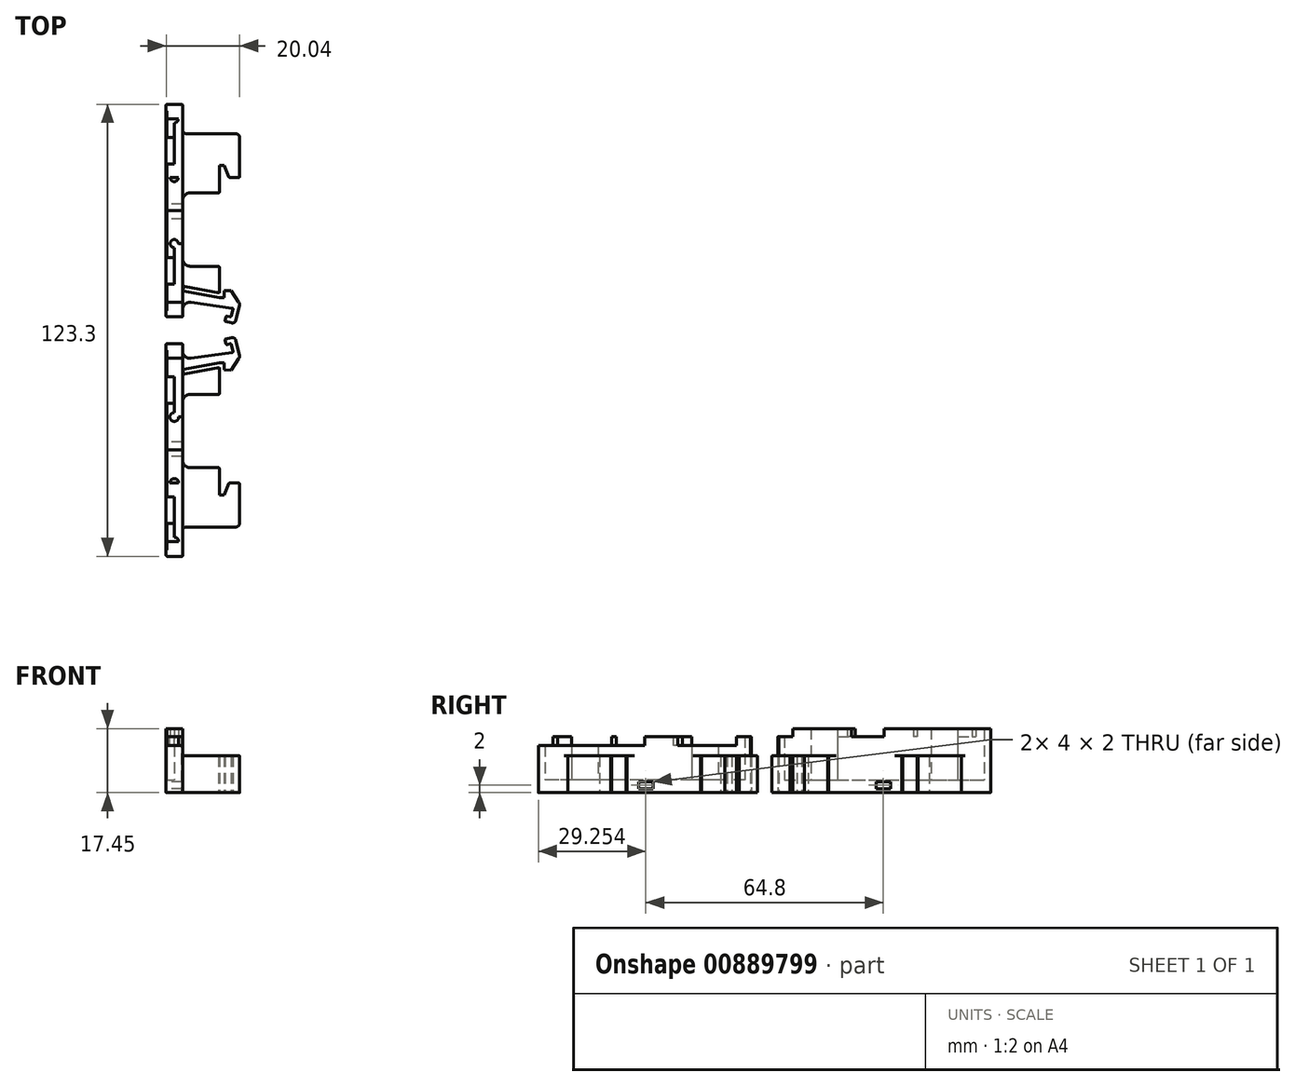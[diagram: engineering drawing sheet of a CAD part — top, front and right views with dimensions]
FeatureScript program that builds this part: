
annotation { "Feature Type Name" : "Feature", "Feature Type Description" : "" }
export const myFeature = defineFeature(function(context is Context, id is Id, definition is map)
    precondition{}
    {
        {
            var Q0;
            Q0=qCreatedBy(makeId("Top.planeOp"),FACE);
            var sketch = newSketch(context, id + "F0", { "sketchPlane" : qUnion([Q0])});
            skLineSegment(sketch, "E0.0", {"start": v(-29.42, 4.4) * mm, "end": v(-29.42, 61.9) * mm});
            skLineSegment(sketch, "E1.0", {"start": v(-29.17, 62.14) * mm, "end": v(-25.17, 62.14) * mm});
            skLineSegment(sketch, "E2.0", {"start": v(-24.92, 55.14) * mm, "end": v(-24.92, 61.9) * mm});
            skLineSegment(sketch, "E3.0", {"start": v(-10.42, 54.14) * mm, "end": v(-23.92, 54.14) * mm});
            skLineSegment(sketch, "E4.0", {"start": v(-9.42, 42.4) * mm, "end": v(-9.42, 53.14) * mm});
            skLineSegment(sketch, "E5.0", {"start": v(-12.07, 42.14) * mm, "end": v(-9.74, 42.14) * mm});
            skLineSegment(sketch, "E6.0", {"start": v(-13.67, 45.45) * mm, "end": v(-12.3, 42.3) * mm});
            skLineSegment(sketch, "E7.0", {"start": v(-14.92, 45.45) * mm, "end": v(-13.67, 45.45) * mm});
            skLineSegment(sketch, "E8.0", {"start": v(-14.92, 38.22) * mm, "end": v(-14.92, 45.45) * mm});
            skLineSegment(sketch, "E9.0", {"start": v(-15.11, 37.97) * mm, "end": v(-22.92, 37.97) * mm});
            skLineSegment(sketch, "E10.0", {"start": v(-24.92, 35.97) * mm, "end": v(-24.92, 19.97) * mm});
            skLineSegment(sketch, "E11.0", {"start": v(-15.11, 17.97) * mm, "end": v(-22.92, 17.97) * mm});
            skLineSegment(sketch, "E12.0", {"start": v(-14.92, 10.64) * mm, "end": v(-14.92, 17.72) * mm});
            skLineSegment(sketch, "E13.0", {"start": v(-14.92, 10.64) * mm, "end": v(-24.39, 12.43) * mm});
            skLineSegment(sketch, "E14.0", {"start": v(-24.82, 11.5) * mm, "end": v(-24.68, 12.23) * mm});
            skLineSegment(sketch, "E15.0", {"start": v(-14.92, 9.37) * mm, "end": v(-24.62, 11.2) * mm});
            skLineSegment(sketch, "E16.0", {"start": v(-13.67, 9.37) * mm, "end": v(-14.92, 9.37) * mm});
            skLineSegment(sketch, "E17.0", {"start": v(-13.67, 11.3) * mm, "end": v(-13.67, 9.37) * mm});
            skLineSegment(sketch, "E18.0", {"start": v(-11.67, 11.34) * mm, "end": v(-13.67, 11.3) * mm});
            skLineSegment(sketch, "E19.0", {"start": v(-11.67, 11.34) * mm, "end": v(-9.66, 8.18) * mm});
            skLineSegment(sketch, "E20.0", {"start": v(-9.38, 7.4) * mm, "end": v(-10.41, 3.24) * mm});
            skLineSegment(sketch, "E21.0", {"start": v(-11.62, 2.5) * mm, "end": v(-13.2, 2.9) * mm});
            skLineSegment(sketch, "E22.0", {"start": v(-13.38, 3.2) * mm, "end": v(-13.14, 4.17) * mm});
            skLineSegment(sketch, "E23.0", {"start": v(-12.83, 4.35) * mm, "end": v(-12, 4.14) * mm});
            skLineSegment(sketch, "E24.0", {"start": v(-11.69, 4.33) * mm, "end": v(-11.21, 6.24) * mm});
            skLineSegment(sketch, "E25.0", {"start": v(-22.65, 8.12) * mm, "end": v(-11.42, 6.55) * mm});
            skLineSegment(sketch, "E26.0", {"start": v(-24.92, 6.14) * mm, "end": v(-24.92, 4.4) * mm});
            skLineSegment(sketch, "E27.0", {"start": v(-25.26, 4.14) * mm, "end": v(-29.17, 4.14) * mm});
            skArc(sketch, "E28.0", {"start": v(-29.17, 62.14) * mm, "mid": v(-29.35, 62.07) * mm, "end": v(-29.42, 61.9) * mm});
            skArc(sketch, "E29.0", {"start": v(-24.92, 61.9) * mm, "mid": v(-25, 62.07) * mm, "end": v(-25.17, 62.14) * mm});
            skArc(sketch, "E30.0", {"start": v(-24.92, 55.14) * mm, "mid": v(-24.63, 54.44) * mm, "end": v(-23.92, 54.14) * mm});
            skArc(sketch, "E31.0", {"start": v(-9.42, 53.14) * mm, "mid": v(-9.72, 53.85) * mm, "end": v(-10.42, 54.14) * mm});
            skArc(sketch, "E32.0", {"start": v(-9.74, 42.14) * mm, "mid": v(-9.52, 42.2) * mm, "end": v(-9.42, 42.4) * mm});
            skArc(sketch, "E33.0", {"start": v(-12.3, 42.3) * mm, "mid": v(-12.2, 42.18) * mm, "end": v(-12.07, 42.14) * mm});
            skArc(sketch, "E34.0", {"start": v(-15.11, 37.97) * mm, "mid": v(-14.97, 38.07) * mm, "end": v(-14.92, 38.22) * mm});
            skArc(sketch, "E35.0", {"start": v(-22.92, 37.97) * mm, "mid": v(-24.34, 37.39) * mm, "end": v(-24.92, 35.97) * mm});
            skArc(sketch, "E36.0", {"start": v(-24.92, 19.97) * mm, "mid": v(-24.34, 18.56) * mm, "end": v(-22.92, 17.97) * mm});
            skArc(sketch, "E37.0", {"start": v(-14.92, 17.72) * mm, "mid": v(-14.97, 17.88) * mm, "end": v(-15.11, 17.97) * mm});
            skArc(sketch, "E38.0", {"start": v(-24.39, 12.43) * mm, "mid": v(-24.58, 12.39) * mm, "end": v(-24.68, 12.23) * mm});
            skArc(sketch, "E39.0", {"start": v(-24.82, 11.5) * mm, "mid": v(-24.78, 11.3) * mm, "end": v(-24.62, 11.2) * mm});
            skArc(sketch, "E40.0", {"start": v(-9.38, 7.4) * mm, "mid": v(-9.43, 7.82) * mm, "end": v(-9.66, 8.18) * mm});
            skArc(sketch, "E41.0", {"start": v(-11.62, 2.5) * mm, "mid": v(-10.87, 2.62) * mm, "end": v(-10.41, 3.24) * mm});
            skArc(sketch, "E42.0", {"start": v(-13.38, 3.2) * mm, "mid": v(-13.35, 3.01) * mm, "end": v(-13.2, 2.9) * mm});
            skArc(sketch, "E43.0", {"start": v(-12.83, 4.35) * mm, "mid": v(-13.02, 4.32) * mm, "end": v(-13.14, 4.17) * mm});
            skArc(sketch, "E44.0", {"start": v(-12, 4.14) * mm, "mid": v(-11.8, 4.17) * mm, "end": v(-11.69, 4.33) * mm});
            skArc(sketch, "E45.0", {"start": v(-11.21, 6.24) * mm, "mid": v(-11.25, 6.44) * mm, "end": v(-11.42, 6.55) * mm});
            skArc(sketch, "E46.0", {"start": v(-22.65, 8.12) * mm, "mid": v(-24.24, 7.65) * mm, "end": v(-24.92, 6.14) * mm});
            skArc(sketch, "E47.0", {"start": v(-25.26, 4.14) * mm, "mid": v(-25.02, 4.18) * mm, "end": v(-24.92, 4.4) * mm});
            skArc(sketch, "E48.0", {"start": v(-29.42, 4.4) * mm, "mid": v(-29.35, 4.22) * mm, "end": v(-29.17, 4.14) * mm});
            skLineSegment(sketch, "E49", {"start": v(-24.92, 61.9) * mm, "end": v(-24.92, 4.4) * mm});
            skLineSegment(sketch, "E50", {"start": v(-29.42, 4.4) * mm, "end": v(-29.42, 5.9) * mm});
            skLineSegment(sketch, "E51", {"start": v(-29.42, 5.9) * mm, "end": v(-29.17, 5.9) * mm});
            skLineSegment(sketch, "E52", {"start": v(-29.17, 5.9) * mm, "end": v(-29.17, 60.4) * mm});
            skLineSegment(sketch, "E53", {"start": v(-29.17, 60.4) * mm, "end": v(-29.42, 60.4) * mm});
            skLineSegment(sketch, "E54", {"start": v(-29.42, 4.4) * mm, "end": v(-29.42, 13.14) * mm});
            skLineSegment(sketch, "E55", {"start": v(-29.42, 13.14) * mm, "end": v(-27.17, 13.14) * mm});
            skLineSegment(sketch, "E56", {"start": v(-27.17, 13.14) * mm, "end": v(-27.17, 20.4) * mm});
            skLineSegment(sketch, "E57", {"start": v(-27.17, 20.4) * mm, "end": v(-29.42, 20.4) * mm});
            skLineSegment(sketch, "E58", {"start": v(-29.42, 20.4) * mm, "end": v(-29.42, 45.9) * mm});
            skLineSegment(sketch, "E59", {"start": v(-29.42, 45.9) * mm, "end": v(-27.17, 45.9) * mm});
            skLineSegment(sketch, "E60", {"start": v(-27.17, 45.9) * mm, "end": v(-27.17, 53.14) * mm});
            skLineSegment(sketch, "E61", {"start": v(-27.17, 53.14) * mm, "end": v(-29.42, 53.14) * mm});
            skSolve(sketch);
        }
        {
            var Q0;
            Q0=makeQuery(id+"F0.imprint","IMPRINT",FACE,{"disambiguationData":[TD([[makeQuery(id+"F0.imprint","IMPRINT",EDGE,{"derivedFrom":sQuery(id+"F0.wireOp",EDGE,"E3.0")}),1.0]])]});
            var Q1;
            Q1=makeQuery(id+"F0.imprint","IMPRINT",FACE,{"disambiguationData":[TD([[makeQuery(id+"F0.imprint","IMPRINT",EDGE,{"derivedFrom":sQuery(id+"F0.wireOp",EDGE,"E0.0")}),-1.0]])]});
            var Q2;
            Q2=makeQuery(id+"F0.imprint","IMPRINT",FACE,{"disambiguationData":[TD([[makeQuery(id+"F0.imprint","IMPRINT",EDGE,{"derivedFrom":sQuery(id+"F0.wireOp",EDGE,"E11.0")}),1.0]])]});
            var Q3;
            {var subQ0=sQuery(id+"F0.wireOp",EDGE,"E51");Q3=makeQuery(id+"F0.imprint","IMPRINT",FACE,{"disambiguationData":[TD([[makeQuery(id+"F0.imprint","IMPRINT",EDGE,{"derivedFrom":subQ0}),1.0]])]});}
            var Q4;
            Q4=makeQuery(id+"F0.imprint","IMPRINT",FACE,{"disambiguationData":[TD([[makeQuery(id+"F0.imprint","IMPRINT",EDGE,{"derivedFrom":sQuery(id+"F0.wireOp",EDGE,"E1.0")}),-1.0]])]});
            var Q5;
            {var subQ5=sQuery(id+"F0.wireOp",EDGE,"CiznJIct-Pn10-4pcS-3v3k-Jn6uBiTixD0h");Q5=makeQuery(id+"F0.imprint","IMPRINT",FACE,{"disambiguationData":[TD([[makeQuery(id+"F0.imprint","IMPRINT",EDGE,{"derivedFrom":subQ5}),1.0]])]});}
            var Q6;
            {var subQ5=sQuery(id+"F0.wireOp",EDGE,"xp5viDYF-1sKM-JXdj-ab4I-l8p1jcBwP8dv");Q6=makeQuery(id+"F0.imprint","IMPRINT",FACE,{"disambiguationData":[TD([[makeQuery(id+"F0.imprint","IMPRINT",EDGE,{"derivedFrom":subQ5}),1.0]])]});}
            var Q7;
            {var subQ5=sQuery(id+"F0.wireOp",EDGE,"eO4NTHjU-XLBs-ehTP-7UjW-MYbdzHAm4Ady");Q7=makeQuery(id+"F0.imprint","IMPRINT",FACE,{"disambiguationData":[TD([[makeQuery(id+"F0.imprint","IMPRINT",EDGE,{"derivedFrom":subQ5}),-1.0]])]});}
            var Q8;
            {var subQ5=sQuery(id+"F0.wireOp",EDGE,"E56");Q8=makeQuery(id+"F0.imprint","IMPRINT",FACE,{"disambiguationData":[TD([[makeQuery(id+"F0.imprint","IMPRINT",EDGE,{"derivedFrom":subQ5}),1.0]])]});}
            var Q9;
            {var subQ5=sQuery(id+"F0.wireOp",EDGE,"E60");Q9=makeQuery(id+"F0.imprint","IMPRINT",FACE,{"disambiguationData":[TD([[makeQuery(id+"F0.imprint","IMPRINT",EDGE,{"derivedFrom":subQ5}),1.0]])]});}
            var Q10;
            {var subQ5=sQuery(id+"F0.wireOp",EDGE,"E58");Q10=makeQuery(id+"F0.imprint","IMPRINT",FACE,{"disambiguationData":[TD([[makeQuery(id+"F0.imprint","IMPRINT",EDGE,{"derivedFrom":subQ5}),-1.0]])]});}
            extrude(context, id + "F1", {"entities" : qUnion([Q0, Q1, Q2, Q3, Q4, Q5, Q6, Q7, Q8, Q9, Q10]), "depth" : 3.5 * mm, "offsetDistance" : 25 * mm});
        }
        {
            var Q0;
            Q0=makeQuery(id+"F1.opExtrude","SWEPT_FACE",FACE,{"disambiguationData":[OSD([sQuery(id+"F0.wireOp",EDGE,"E0.0")])]});
            var sketch = newSketch(context, id + "F2", { "sketchPlane" : qUnion([Q0])});
            skLineSegment(sketch, "E62.bottom", {"start": v(-30.9, 1) * mm, "end": v(-34.9, 1) * mm});
            skLineSegment(sketch, "E62.top", {"start": v(-30.9, 3) * mm, "end": v(-34.9, 3) * mm});
            skLineSegment(sketch, "E62.left", {"start": v(-30.9, 1) * mm, "end": v(-30.9, 3) * mm});
            skLineSegment(sketch, "E62.right", {"start": v(-34.9, 1) * mm, "end": v(-34.9, 3) * mm});
            skPoint(sketch, "E62.middle", {"position": v(-32.9, 2) * mm});
            skSolve(sketch);
        }
        {
            var Q0;
            Q0 = qSketchRegion(id + "F2", true);
            extrude(context, id + "F3", {"entities" : qUnion([Q0]), "operationType" : NewBodyOperationType.REMOVE, "oppositeDirection" : true, "depth" : 4.5 * mm, "offsetDistance" : 25 * mm});
        }
        {
            var Q0;
            Q0=makeQuery(id+"F1.opExtrude","CAP_FACE",FACE,{"disambiguationData":[OSD([sQuery(id+"F0.wireOp",EDGE,"E0.0"),sQuery(id+"F0.wireOp",EDGE,"E1.0"),sQuery(id+"F0.wireOp",EDGE,"E3.0"),sQuery(id+"F0.wireOp",EDGE,"E4.0"),sQuery(id+"F0.wireOp",EDGE,"E5.0"),sQuery(id+"F0.wireOp",EDGE,"E6.0"),sQuery(id+"F0.wireOp",EDGE,"E7.0"),sQuery(id+"F0.wireOp",EDGE,"E8.0"),sQuery(id+"F0.wireOp",EDGE,"E9.0"),sQuery(id+"F0.wireOp",EDGE,"E11.0"),sQuery(id+"F0.wireOp",EDGE,"E12.0"),sQuery(id+"F0.wireOp",EDGE,"E13.0"),sQuery(id+"F0.wireOp",EDGE,"E14.0"),sQuery(id+"F0.wireOp",EDGE,"E15.0"),sQuery(id+"F0.wireOp",EDGE,"E16.0"),sQuery(id+"F0.wireOp",EDGE,"E17.0"),sQuery(id+"F0.wireOp",EDGE,"E18.0"),sQuery(id+"F0.wireOp",EDGE,"E19.0"),sQuery(id+"F0.wireOp",EDGE,"E20.0"),sQuery(id+"F0.wireOp",EDGE,"E21.0"),sQuery(id+"F0.wireOp",EDGE,"E22.0"),sQuery(id+"F0.wireOp",EDGE,"E23.0"),sQuery(id+"F0.wireOp",EDGE,"E24.0"),sQuery(id+"F0.wireOp",EDGE,"E25.0"),sQuery(id+"F0.wireOp",EDGE,"E27.0"),sQuery(id+"F0.wireOp",EDGE,"E28.0"),sQuery(id+"F0.wireOp",EDGE,"E29.0"),sQuery(id+"F0.wireOp",EDGE,"E30.0"),sQuery(id+"F0.wireOp",EDGE,"E31.0"),sQuery(id+"F0.wireOp",EDGE,"E32.0"),sQuery(id+"F0.wireOp",EDGE,"E33.0"),sQuery(id+"F0.wireOp",EDGE,"E34.0"),sQuery(id+"F0.wireOp",EDGE,"E35.0"),sQuery(id+"F0.wireOp",EDGE,"E36.0"),sQuery(id+"F0.wireOp",EDGE,"E37.0"),sQuery(id+"F0.wireOp",EDGE,"E38.0"),sQuery(id+"F0.wireOp",EDGE,"E39.0"),sQuery(id+"F0.wireOp",EDGE,"E40.0"),sQuery(id+"F0.wireOp",EDGE,"E41.0"),sQuery(id+"F0.wireOp",EDGE,"E42.0"),sQuery(id+"F0.wireOp",EDGE,"E43.0"),sQuery(id+"F0.wireOp",EDGE,"E44.0"),sQuery(id+"F0.wireOp",EDGE,"E45.0"),sQuery(id+"F0.wireOp",EDGE,"E46.0"),sQuery(id+"F0.wireOp",EDGE,"E47.0"),sQuery(id+"F0.wireOp",EDGE,"E48.0"),sQuery(id+"F0.wireOp",EDGE,"E49"),sQuery(id+"F0.wireOp",EDGE,"E54"),sQuery(id+"F0.wireOp",EDGE,"eO4NTHjU-XLBs-ehTP-7UjW-MYbdzHAm4Ady")])],"isStart":false});
            var sketch = newSketch(context, id + "F4", { "sketchPlane" : qUnion([Q0])});
            skLineSegment(sketch, "E63.0", {"start": v(-29.17, 5.9) * mm, "end": v(-29.17, 60.4) * mm});
            skLineSegment(sketch, "E64.0", {"start": v(-29.42, 5.9) * mm, "end": v(-29.17, 5.9) * mm});
            skLineSegment(sketch, "E65.0", {"start": v(-29.17, 60.4) * mm, "end": v(-29.42, 60.4) * mm});
            skPoint(sketch, "E66.0", {"position": v(-28.3, 54.14) * mm});
            skLineSegment(sketch, "E67.0", {"start": v(-29.42, 13.14) * mm, "end": v(-27.17, 13.14) * mm});
            skLineSegment(sketch, "E68.0", {"start": v(-27.17, 13.14) * mm, "end": v(-27.17, 20.4) * mm});
            skLineSegment(sketch, "E69.0", {"start": v(-27.17, 20.4) * mm, "end": v(-29.42, 20.4) * mm});
            skLineSegment(sketch, "E70.0", {"start": v(-29.42, 45.9) * mm, "end": v(-27.17, 45.9) * mm});
            skLineSegment(sketch, "E71.0", {"start": v(-27.17, 45.9) * mm, "end": v(-27.17, 53.14) * mm});
            skLineSegment(sketch, "E72.0", {"start": v(-27.17, 53.14) * mm, "end": v(-29.42, 53.14) * mm});
            skSolve(sketch);
        }
        {
            var Q0;
            {var subQ12=sQuery(id+"F4.wireOp",EDGE,"E64.0");Q0=makeQuery(id+"F4.imprint","IMPRINT",FACE,{"disambiguationData":[TD([[makeQuery(id+"F4.imprint","IMPRINT",EDGE,{"derivedFrom":subQ12}),-1.0]])]});}
            extrude(context, id + "F5", {"entities" : qUnion([Q0]), "operationType" : NewBodyOperationType.ADD, "depth" : 6.5 * mm, "offsetDistance" : 25 * mm});
        }
        {
            var Q0;
            Q0=makeQuery(id+"F5.opExtrude","CAP_FACE",FACE,{"disambiguationData":[OSD([sQuery(id+"F0.wireOp",EDGE,"E0.0"),sQuery(id+"F0.wireOp",EDGE,"E1.0"),sQuery(id+"F0.wireOp",EDGE,"E3.0"),sQuery(id+"F0.wireOp",EDGE,"E4.0"),sQuery(id+"F0.wireOp",EDGE,"E5.0"),sQuery(id+"F0.wireOp",EDGE,"E6.0"),sQuery(id+"F0.wireOp",EDGE,"E7.0"),sQuery(id+"F0.wireOp",EDGE,"E8.0"),sQuery(id+"F0.wireOp",EDGE,"E9.0"),sQuery(id+"F0.wireOp",EDGE,"E11.0"),sQuery(id+"F0.wireOp",EDGE,"E12.0"),sQuery(id+"F0.wireOp",EDGE,"E13.0"),sQuery(id+"F0.wireOp",EDGE,"E14.0"),sQuery(id+"F0.wireOp",EDGE,"E15.0"),sQuery(id+"F0.wireOp",EDGE,"E16.0"),sQuery(id+"F0.wireOp",EDGE,"E17.0"),sQuery(id+"F0.wireOp",EDGE,"E18.0"),sQuery(id+"F0.wireOp",EDGE,"E19.0"),sQuery(id+"F0.wireOp",EDGE,"E20.0"),sQuery(id+"F0.wireOp",EDGE,"E21.0"),sQuery(id+"F0.wireOp",EDGE,"E22.0"),sQuery(id+"F0.wireOp",EDGE,"E23.0"),sQuery(id+"F0.wireOp",EDGE,"E24.0"),sQuery(id+"F0.wireOp",EDGE,"E25.0"),sQuery(id+"F0.wireOp",EDGE,"E27.0"),sQuery(id+"F0.wireOp",EDGE,"E28.0"),sQuery(id+"F0.wireOp",EDGE,"E29.0"),sQuery(id+"F0.wireOp",EDGE,"E30.0"),sQuery(id+"F0.wireOp",EDGE,"E31.0"),sQuery(id+"F0.wireOp",EDGE,"E32.0"),sQuery(id+"F0.wireOp",EDGE,"E33.0"),sQuery(id+"F0.wireOp",EDGE,"E34.0"),sQuery(id+"F0.wireOp",EDGE,"E35.0"),sQuery(id+"F0.wireOp",EDGE,"E36.0"),sQuery(id+"F0.wireOp",EDGE,"E37.0"),sQuery(id+"F0.wireOp",EDGE,"E38.0"),sQuery(id+"F0.wireOp",EDGE,"E39.0"),sQuery(id+"F0.wireOp",EDGE,"E40.0"),sQuery(id+"F0.wireOp",EDGE,"E41.0"),sQuery(id+"F0.wireOp",EDGE,"E42.0"),sQuery(id+"F0.wireOp",EDGE,"E43.0"),sQuery(id+"F0.wireOp",EDGE,"E44.0"),sQuery(id+"F0.wireOp",EDGE,"E45.0"),sQuery(id+"F0.wireOp",EDGE,"E46.0"),sQuery(id+"F0.wireOp",EDGE,"E47.0"),sQuery(id+"F0.wireOp",EDGE,"E48.0"),sQuery(id+"F0.wireOp",EDGE,"E49"),sQuery(id+"F0.wireOp",EDGE,"E54"),sQuery(id+"F0.wireOp",EDGE,"eO4NTHjU-XLBs-ehTP-7UjW-MYbdzHAm4Ady"),sQuery(id+"F4.wireOp",EDGE,"E63.0"),sQuery(id+"F4.wireOp",EDGE,"E64.0"),sQuery(id+"F4.wireOp",EDGE,"E65.0"),sQuery(id+"F4.wireOp",EDGE,"70bcd36a-43df-4478-8c9e-d5456ba7c832.0"),sQuery(id+"F4.wireOp",EDGE,"bf217143-492d-4eb7-9494-7eafc8b65626.0"),sQuery(id+"F4.wireOp",EDGE,"a46a1f45-c3d6-4197-9e03-8490d21bd8d4.0"),sQuery(id+"F4.wireOp",EDGE,"a334625e-ec4d-4089-b1dc-05afd864aa37.0"),sQuery(id+"F4.wireOp",EDGE,"6e801660-dba5-42c4-9896-378528af69a1.0"),sQuery(id+"F4.wireOp",EDGE,"c2987821-0ad2-4387-8c91-164f40ca8063.0")])],"isStart":false});
            var sketch = newSketch(context, id + "F6", { "sketchPlane" : qUnion([Q0])});
            skLineSegment(sketch, "E73.0", {"start": v(-24.92, 61.9) * mm, "end": v(-24.92, 4.4) * mm});
            skSolve(sketch);
        }
        {
            var Q0;
            {var subQ8=sQuery(id+"F4.wireOp",EDGE,"E64.0");Q0=makeQuery(id+"F6.imprint","IMPRINT",FACE,{"disambiguationData":[TD([[makeQuery(id+"F6.imprint","IMPRINT",EDGE,{"derivedFrom":makeQuery(id+"F5.opExtrude","CAP_EDGE",EDGE,{"disambiguationData":[OSD([subQ8])],"isStart":false})}),-1.0]])]});}
            extrude(context, id + "F7", {"entities" : qUnion([Q0]), "operationType" : NewBodyOperationType.ADD, "depth" : 5.25 * mm, "offsetDistance" : 25 * mm});
        }
        {
            var Q0;
            Q0=makeQuery(id+"F1.opExtrude","SWEPT_BODY",BODY,{"disambiguationData":[OSD([sQuery(id+"F0.wireOp",EDGE,"E0.0"),sQuery(id+"F0.wireOp",EDGE,"E1.0"),sQuery(id+"F0.wireOp",EDGE,"E3.0"),sQuery(id+"F0.wireOp",EDGE,"E4.0"),sQuery(id+"F0.wireOp",EDGE,"E5.0"),sQuery(id+"F0.wireOp",EDGE,"E6.0"),sQuery(id+"F0.wireOp",EDGE,"E7.0"),sQuery(id+"F0.wireOp",EDGE,"E8.0"),sQuery(id+"F0.wireOp",EDGE,"E9.0"),sQuery(id+"F0.wireOp",EDGE,"E11.0"),sQuery(id+"F0.wireOp",EDGE,"E12.0"),sQuery(id+"F0.wireOp",EDGE,"E13.0"),sQuery(id+"F0.wireOp",EDGE,"E14.0"),sQuery(id+"F0.wireOp",EDGE,"E15.0"),sQuery(id+"F0.wireOp",EDGE,"E16.0"),sQuery(id+"F0.wireOp",EDGE,"E17.0"),sQuery(id+"F0.wireOp",EDGE,"E18.0"),sQuery(id+"F0.wireOp",EDGE,"E19.0"),sQuery(id+"F0.wireOp",EDGE,"E20.0"),sQuery(id+"F0.wireOp",EDGE,"E21.0"),sQuery(id+"F0.wireOp",EDGE,"E22.0"),sQuery(id+"F0.wireOp",EDGE,"E23.0"),sQuery(id+"F0.wireOp",EDGE,"E24.0"),sQuery(id+"F0.wireOp",EDGE,"E25.0"),sQuery(id+"F0.wireOp",EDGE,"E27.0"),sQuery(id+"F0.wireOp",EDGE,"E28.0"),sQuery(id+"F0.wireOp",EDGE,"E29.0"),sQuery(id+"F0.wireOp",EDGE,"E30.0"),sQuery(id+"F0.wireOp",EDGE,"E31.0"),sQuery(id+"F0.wireOp",EDGE,"E32.0"),sQuery(id+"F0.wireOp",EDGE,"E33.0"),sQuery(id+"F0.wireOp",EDGE,"E34.0"),sQuery(id+"F0.wireOp",EDGE,"E35.0"),sQuery(id+"F0.wireOp",EDGE,"E36.0"),sQuery(id+"F0.wireOp",EDGE,"E37.0"),sQuery(id+"F0.wireOp",EDGE,"E38.0"),sQuery(id+"F0.wireOp",EDGE,"E39.0"),sQuery(id+"F0.wireOp",EDGE,"E40.0"),sQuery(id+"F0.wireOp",EDGE,"E41.0"),sQuery(id+"F0.wireOp",EDGE,"E42.0"),sQuery(id+"F0.wireOp",EDGE,"E43.0"),sQuery(id+"F0.wireOp",EDGE,"E44.0"),sQuery(id+"F0.wireOp",EDGE,"E45.0"),sQuery(id+"F0.wireOp",EDGE,"E46.0"),sQuery(id+"F0.wireOp",EDGE,"E47.0"),sQuery(id+"F0.wireOp",EDGE,"E48.0"),sQuery(id+"F0.wireOp",EDGE,"E49"),sQuery(id+"F0.wireOp",EDGE,"E54"),sQuery(id+"F0.wireOp",EDGE,"eO4NTHjU-XLBs-ehTP-7UjW-MYbdzHAm4Ady")])]});
            var Q1;
            Q1=makeQuery(id+"F7.opExtrude","CAP_FACE",FACE,{"disambiguationData":[OSD([sQuery(id+"F0.wireOp",EDGE,"E0.0"),sQuery(id+"F0.wireOp",EDGE,"E1.0"),sQuery(id+"F0.wireOp",EDGE,"E27.0"),sQuery(id+"F0.wireOp",EDGE,"E28.0"),sQuery(id+"F0.wireOp",EDGE,"E29.0"),sQuery(id+"F0.wireOp",EDGE,"E47.0"),sQuery(id+"F0.wireOp",EDGE,"E48.0"),sQuery(id+"F0.wireOp",EDGE,"E54"),sQuery(id+"F0.wireOp",EDGE,"eO4NTHjU-XLBs-ehTP-7UjW-MYbdzHAm4Ady"),sQuery(id+"F4.wireOp",EDGE,"E63.0"),sQuery(id+"F4.wireOp",EDGE,"E64.0"),sQuery(id+"F4.wireOp",EDGE,"E65.0"),sQuery(id+"F4.wireOp",EDGE,"70bcd36a-43df-4478-8c9e-d5456ba7c832.0"),sQuery(id+"F4.wireOp",EDGE,"bf217143-492d-4eb7-9494-7eafc8b65626.0"),sQuery(id+"F4.wireOp",EDGE,"a46a1f45-c3d6-4197-9e03-8490d21bd8d4.0"),sQuery(id+"F4.wireOp",EDGE,"a334625e-ec4d-4089-b1dc-05afd864aa37.0"),sQuery(id+"F4.wireOp",EDGE,"6e801660-dba5-42c4-9896-378528af69a1.0"),sQuery(id+"F4.wireOp",EDGE,"c2987821-0ad2-4387-8c91-164f40ca8063.0"),sQuery(id+"F6.wireOp",EDGE,"E73.0")])],"isStart":false});
            mirror(context, id + "F8", {"entities" : qUnion([Q0]), "mirrorPlane" : qUnion([Q1])});
        }
        {
            var Q0;
            Q0=makeQuery(id+"F8.opPattern","COPY",BODY,{"derivedFrom":makeQuery(id+"F1.opExtrude","SWEPT_BODY",BODY,{"disambiguationData":[OSD([sQuery(id+"F0.wireOp",EDGE,"E0.0"),sQuery(id+"F0.wireOp",EDGE,"E1.0"),sQuery(id+"F0.wireOp",EDGE,"E3.0"),sQuery(id+"F0.wireOp",EDGE,"E4.0"),sQuery(id+"F0.wireOp",EDGE,"E5.0"),sQuery(id+"F0.wireOp",EDGE,"E6.0"),sQuery(id+"F0.wireOp",EDGE,"E7.0"),sQuery(id+"F0.wireOp",EDGE,"E8.0"),sQuery(id+"F0.wireOp",EDGE,"E9.0"),sQuery(id+"F0.wireOp",EDGE,"E11.0"),sQuery(id+"F0.wireOp",EDGE,"E12.0"),sQuery(id+"F0.wireOp",EDGE,"E13.0"),sQuery(id+"F0.wireOp",EDGE,"E14.0"),sQuery(id+"F0.wireOp",EDGE,"E15.0"),sQuery(id+"F0.wireOp",EDGE,"E16.0"),sQuery(id+"F0.wireOp",EDGE,"E17.0"),sQuery(id+"F0.wireOp",EDGE,"E18.0"),sQuery(id+"F0.wireOp",EDGE,"E19.0"),sQuery(id+"F0.wireOp",EDGE,"E20.0"),sQuery(id+"F0.wireOp",EDGE,"E21.0"),sQuery(id+"F0.wireOp",EDGE,"E22.0"),sQuery(id+"F0.wireOp",EDGE,"E23.0"),sQuery(id+"F0.wireOp",EDGE,"E24.0"),sQuery(id+"F0.wireOp",EDGE,"E25.0"),sQuery(id+"F0.wireOp",EDGE,"E27.0"),sQuery(id+"F0.wireOp",EDGE,"E28.0"),sQuery(id+"F0.wireOp",EDGE,"E29.0"),sQuery(id+"F0.wireOp",EDGE,"E30.0"),sQuery(id+"F0.wireOp",EDGE,"E31.0"),sQuery(id+"F0.wireOp",EDGE,"E32.0"),sQuery(id+"F0.wireOp",EDGE,"E33.0"),sQuery(id+"F0.wireOp",EDGE,"E34.0"),sQuery(id+"F0.wireOp",EDGE,"E35.0"),sQuery(id+"F0.wireOp",EDGE,"E36.0"),sQuery(id+"F0.wireOp",EDGE,"E37.0"),sQuery(id+"F0.wireOp",EDGE,"E38.0"),sQuery(id+"F0.wireOp",EDGE,"E39.0"),sQuery(id+"F0.wireOp",EDGE,"E40.0"),sQuery(id+"F0.wireOp",EDGE,"E41.0"),sQuery(id+"F0.wireOp",EDGE,"E42.0"),sQuery(id+"F0.wireOp",EDGE,"E43.0"),sQuery(id+"F0.wireOp",EDGE,"E44.0"),sQuery(id+"F0.wireOp",EDGE,"E45.0"),sQuery(id+"F0.wireOp",EDGE,"E46.0"),sQuery(id+"F0.wireOp",EDGE,"E47.0"),sQuery(id+"F0.wireOp",EDGE,"E48.0"),sQuery(id+"F0.wireOp",EDGE,"E49"),sQuery(id+"F0.wireOp",EDGE,"E54"),sQuery(id+"F0.wireOp",EDGE,"eO4NTHjU-XLBs-ehTP-7UjW-MYbdzHAm4Ady")])]}),"instanceName":"1"});
            var Q1;
            Q1=makeQuery(id+"F7.opExtrude","CAP_EDGE",EDGE,{"disambiguationData":[OSD([sQuery(id+"F0.wireOp",EDGE,"E1.0")])],"isStart":false});
            transform(context, id + "F9", {"entities" : qUnion([Q0]), "transformType" : TransformType.ROTATION, "transformAxis" : qUnion([Q1]), "angle" : 180 * degree, "makeCopy" : false});
        }
        {
            var Q0;
            Q0=makeQuery(id+"F8.opPattern","COPY",BODY,{"derivedFrom":makeQuery(id+"F1.opExtrude","SWEPT_BODY",BODY,{"disambiguationData":[OSD([sQuery(id+"F0.wireOp",EDGE,"E0.0"),sQuery(id+"F0.wireOp",EDGE,"E1.0"),sQuery(id+"F0.wireOp",EDGE,"E3.0"),sQuery(id+"F0.wireOp",EDGE,"E4.0"),sQuery(id+"F0.wireOp",EDGE,"E5.0"),sQuery(id+"F0.wireOp",EDGE,"E6.0"),sQuery(id+"F0.wireOp",EDGE,"E7.0"),sQuery(id+"F0.wireOp",EDGE,"E8.0"),sQuery(id+"F0.wireOp",EDGE,"E9.0"),sQuery(id+"F0.wireOp",EDGE,"E11.0"),sQuery(id+"F0.wireOp",EDGE,"E12.0"),sQuery(id+"F0.wireOp",EDGE,"E13.0"),sQuery(id+"F0.wireOp",EDGE,"E14.0"),sQuery(id+"F0.wireOp",EDGE,"E15.0"),sQuery(id+"F0.wireOp",EDGE,"E16.0"),sQuery(id+"F0.wireOp",EDGE,"E17.0"),sQuery(id+"F0.wireOp",EDGE,"E18.0"),sQuery(id+"F0.wireOp",EDGE,"E19.0"),sQuery(id+"F0.wireOp",EDGE,"E20.0"),sQuery(id+"F0.wireOp",EDGE,"E21.0"),sQuery(id+"F0.wireOp",EDGE,"E22.0"),sQuery(id+"F0.wireOp",EDGE,"E23.0"),sQuery(id+"F0.wireOp",EDGE,"E24.0"),sQuery(id+"F0.wireOp",EDGE,"E25.0"),sQuery(id+"F0.wireOp",EDGE,"E27.0"),sQuery(id+"F0.wireOp",EDGE,"E28.0"),sQuery(id+"F0.wireOp",EDGE,"E29.0"),sQuery(id+"F0.wireOp",EDGE,"E30.0"),sQuery(id+"F0.wireOp",EDGE,"E31.0"),sQuery(id+"F0.wireOp",EDGE,"E32.0"),sQuery(id+"F0.wireOp",EDGE,"E33.0"),sQuery(id+"F0.wireOp",EDGE,"E34.0"),sQuery(id+"F0.wireOp",EDGE,"E35.0"),sQuery(id+"F0.wireOp",EDGE,"E36.0"),sQuery(id+"F0.wireOp",EDGE,"E37.0"),sQuery(id+"F0.wireOp",EDGE,"E38.0"),sQuery(id+"F0.wireOp",EDGE,"E39.0"),sQuery(id+"F0.wireOp",EDGE,"E40.0"),sQuery(id+"F0.wireOp",EDGE,"E41.0"),sQuery(id+"F0.wireOp",EDGE,"E42.0"),sQuery(id+"F0.wireOp",EDGE,"E43.0"),sQuery(id+"F0.wireOp",EDGE,"E44.0"),sQuery(id+"F0.wireOp",EDGE,"E45.0"),sQuery(id+"F0.wireOp",EDGE,"E46.0"),sQuery(id+"F0.wireOp",EDGE,"E47.0"),sQuery(id+"F0.wireOp",EDGE,"E48.0"),sQuery(id+"F0.wireOp",EDGE,"E49"),sQuery(id+"F0.wireOp",EDGE,"E54"),sQuery(id+"F0.wireOp",EDGE,"eO4NTHjU-XLBs-ehTP-7UjW-MYbdzHAm4Ady")])]}),"instanceName":"1"});
            transform(context, id + "F10", {"entities" : qUnion([Q0]), "transformType" : TransformType.TRANSLATION_3D, "dx" : 0 * mm, "dy" : -123.3 * mm, "dz" : 0 * mm, "makeCopy" : false});
        }
        {
            var Q0;
            Q0=makeQuery(id+"F7.opExtrude","CAP_FACE",FACE,{"disambiguationData":[OSD([sQuery(id+"F0.wireOp",EDGE,"E0.0"),sQuery(id+"F0.wireOp",EDGE,"E1.0"),sQuery(id+"F0.wireOp",EDGE,"E27.0"),sQuery(id+"F0.wireOp",EDGE,"E28.0"),sQuery(id+"F0.wireOp",EDGE,"E29.0"),sQuery(id+"F0.wireOp",EDGE,"E47.0"),sQuery(id+"F0.wireOp",EDGE,"E48.0"),sQuery(id+"F0.wireOp",EDGE,"E54"),sQuery(id+"F0.wireOp",EDGE,"eO4NTHjU-XLBs-ehTP-7UjW-MYbdzHAm4Ady"),sQuery(id+"F4.wireOp",EDGE,"E63.0"),sQuery(id+"F4.wireOp",EDGE,"E64.0"),sQuery(id+"F4.wireOp",EDGE,"E65.0"),sQuery(id+"F4.wireOp",EDGE,"70bcd36a-43df-4478-8c9e-d5456ba7c832.0"),sQuery(id+"F4.wireOp",EDGE,"bf217143-492d-4eb7-9494-7eafc8b65626.0"),sQuery(id+"F4.wireOp",EDGE,"a46a1f45-c3d6-4197-9e03-8490d21bd8d4.0"),sQuery(id+"F4.wireOp",EDGE,"a334625e-ec4d-4089-b1dc-05afd864aa37.0"),sQuery(id+"F4.wireOp",EDGE,"6e801660-dba5-42c4-9896-378528af69a1.0"),sQuery(id+"F4.wireOp",EDGE,"c2987821-0ad2-4387-8c91-164f40ca8063.0"),sQuery(id+"F6.wireOp",EDGE,"E73.0")])],"isStart":false});
            var sketch = newSketch(context, id + "F11", { "sketchPlane" : qUnion([Q0])});
            skLineSegment(sketch, "E74", {"start": v(-27.22, 4.14) * mm, "end": v(-27.22, 62.14) * mm});
            skLineSegment(sketch, "E75", {"start": v(-24.92, 8.14) * mm, "end": v(-29.17, 8.14) * mm});
            skPoint(sketch, "E75.endSnap0", {"position": v(-29.17, 9.52) * mm});
            skLineSegment(sketch, "E76", {"start": v(-24.92, 33.14) * mm, "end": v(-29.17, 33.14) * mm});
            skLineSegment(sketch, "E77", {"start": v(-24.92, 58.14) * mm, "end": v(-29.17, 58.14) * mm});
            skPoint(sketch, "E78", {"position": v(-27.22, 8.14) * mm});
            skPoint(sketch, "E79", {"position": v(-27.22, 33.14) * mm});
            skPoint(sketch, "E80", {"position": v(-27.22, 58.14) * mm});
            skCircle(sketch, "E81", {"center": v(-27.22, 58.14) * mm, "radius": 1.1 * mm});
            skCircle(sketch, "E82", {"center": v(-27.22, 33.14) * mm, "radius": 1.1 * mm});
            skCircle(sketch, "E83", {"center": v(-27.22, 8.14) * mm, "radius": 1.1 * mm});
            skLineSegment(sketch, "E84", {"start": v(-29.17, 42.14) * mm, "end": v(-24.92, 42.14) * mm});
            skLineSegment(sketch, "E85", {"start": v(-29.17, 24.14) * mm, "end": v(-24.92, 24.14) * mm});
            skPoint(sketch, "E86", {"position": v(-27.22, 24.14) * mm});
            skPoint(sketch, "E87", {"position": v(-27.22, 42.14) * mm});
            skCircle(sketch, "E88", {"center": v(-27.22, 24.14) * mm, "radius": 1.1 * mm});
            skCircle(sketch, "E89", {"center": v(-27.22, 42.14) * mm, "radius": 1.1 * mm});
            skSolve(sketch);
        }
        {
            var Q0;
            Q0=makeQuery(id+"F8.opPattern","COPY",FACE,{"derivedFrom":makeQuery(id+"F7.opExtrude","CAP_FACE",FACE,{"disambiguationData":[OSD([sQuery(id+"F0.wireOp",EDGE,"E0.0"),sQuery(id+"F0.wireOp",EDGE,"E1.0"),sQuery(id+"F0.wireOp",EDGE,"E27.0"),sQuery(id+"F0.wireOp",EDGE,"E28.0"),sQuery(id+"F0.wireOp",EDGE,"E29.0"),sQuery(id+"F0.wireOp",EDGE,"E47.0"),sQuery(id+"F0.wireOp",EDGE,"E48.0"),sQuery(id+"F0.wireOp",EDGE,"E54"),sQuery(id+"F0.wireOp",EDGE,"eO4NTHjU-XLBs-ehTP-7UjW-MYbdzHAm4Ady"),sQuery(id+"F4.wireOp",EDGE,"E63.0"),sQuery(id+"F4.wireOp",EDGE,"E64.0"),sQuery(id+"F4.wireOp",EDGE,"E65.0"),sQuery(id+"F4.wireOp",EDGE,"70bcd36a-43df-4478-8c9e-d5456ba7c832.0"),sQuery(id+"F4.wireOp",EDGE,"bf217143-492d-4eb7-9494-7eafc8b65626.0"),sQuery(id+"F4.wireOp",EDGE,"a46a1f45-c3d6-4197-9e03-8490d21bd8d4.0"),sQuery(id+"F4.wireOp",EDGE,"a334625e-ec4d-4089-b1dc-05afd864aa37.0"),sQuery(id+"F4.wireOp",EDGE,"6e801660-dba5-42c4-9896-378528af69a1.0"),sQuery(id+"F4.wireOp",EDGE,"c2987821-0ad2-4387-8c91-164f40ca8063.0"),sQuery(id+"F6.wireOp",EDGE,"E73.0")])],"isStart":false}),"instanceName":"1"});
            var sketch = newSketch(context, id + "F12", { "sketchPlane" : qUnion([Q0])});
            skLineSegment(sketch, "E90", {"start": v(-27.22, -3.16) * mm, "end": v(-27.22, -61.16) * mm});
            skLineSegment(sketch, "E91", {"start": v(-24.92, -7.16) * mm, "end": v(-29.17, -7.16) * mm});
            skLineSegment(sketch, "E92", {"start": v(-24.92, -32.16) * mm, "end": v(-29.17, -32.16) * mm});
            skLineSegment(sketch, "E93", {"start": v(-24.92, -57.16) * mm, "end": v(-29.17, -57.16) * mm});
            skPoint(sketch, "E94", {"position": v(-27.22, -57.16) * mm});
            skPoint(sketch, "E95", {"position": v(-27.22, -32.16) * mm});
            skPoint(sketch, "E96", {"position": v(-27.22, -7.16) * mm});
            skCircle(sketch, "E97", {"center": v(-27.22, -57.16) * mm, "radius": 1.2 * mm});
            skCircle(sketch, "E98", {"center": v(-27.22, -32.16) * mm, "radius": 1.2 * mm});
            skCircle(sketch, "E99", {"center": v(-27.22, -7.16) * mm, "radius": 1.2 * mm});
            skLineSegment(sketch, "E100", {"start": v(-29.17, -41.16) * mm, "end": v(-24.92, -41.16) * mm});
            skLineSegment(sketch, "E101", {"start": v(-29.17, -23.16) * mm, "end": v(-24.92, -23.16) * mm});
            skPoint(sketch, "E102", {"position": v(-27.22, -41.16) * mm});
            skPoint(sketch, "E103", {"position": v(-27.22, -23.16) * mm});
            skCircle(sketch, "E104", {"center": v(-27.22, -41.16) * mm, "radius": 1.2 * mm});
            skCircle(sketch, "E105", {"center": v(-27.22, -23.16) * mm, "radius": 1.2 * mm});
            skSolve(sketch);
        }
        {
            var Q0;
            {var subQ0=sQuery(id+"F12.wireOp",EDGE,"E93");var subQ1=sQuery(id+"F12.wireOp",EDGE,"E90");var subQ2=makeQuery(id+"F12.imprint","INTERSECT",VERTEX,{"derivedFrom":[subQ1,subQ0]});Q0=makeQuery(id+"F12.imprint","IMPRINT",FACE,{"disambiguationData":[TD([[makeQuery(id+"F12.imprint","IMPRINT",EDGE,{"disambiguationData":[TD([[subQ2,-1.0]])],"derivedFrom":subQ1}),-1.0]])]});}
            var Q1;
            {var subQ0=sQuery(id+"F12.wireOp",EDGE,"E97");var subQ1=sQuery(id+"F12.wireOp",EDGE,"E90");var subQ2=makeQuery(id+"F12.imprint","INTERSECT",VERTEX,{"disambiguationData":[OD(0.0)],"derivedFrom":[subQ1,subQ0]});Q1=makeQuery(id+"F12.imprint","IMPRINT",FACE,{"disambiguationData":[TD([[makeQuery(id+"F12.imprint","IMPRINT",EDGE,{"disambiguationData":[TD([[subQ2,-1.0]])],"derivedFrom":subQ1}),-1.0]])]});}
            var Q2;
            {var subQ0=sQuery(id+"F12.wireOp",EDGE,"E97");var subQ1=sQuery(id+"F12.wireOp",EDGE,"E90");var subQ2=makeQuery(id+"F12.imprint","INTERSECT",VERTEX,{"disambiguationData":[OD(0.0)],"derivedFrom":[subQ1,subQ0]});Q2=makeQuery(id+"F12.imprint","IMPRINT",FACE,{"disambiguationData":[TD([[makeQuery(id+"F12.imprint","IMPRINT",EDGE,{"disambiguationData":[TD([[subQ2,-1.0]])],"derivedFrom":subQ1}),1.0]])]});}
            var Q3;
            {var subQ0=sQuery(id+"F12.wireOp",EDGE,"E93");var subQ1=sQuery(id+"F12.wireOp",EDGE,"E90");var subQ2=makeQuery(id+"F12.imprint","INTERSECT",VERTEX,{"derivedFrom":[subQ1,subQ0]});Q3=makeQuery(id+"F12.imprint","IMPRINT",FACE,{"disambiguationData":[TD([[makeQuery(id+"F12.imprint","IMPRINT",EDGE,{"disambiguationData":[TD([[subQ2,-1.0]])],"derivedFrom":subQ1}),1.0]])]});}
            var Q4;
            {var subQ0=sQuery(id+"F12.wireOp",EDGE,"E92");var subQ1=sQuery(id+"F12.wireOp",EDGE,"E90");var subQ2=makeQuery(id+"F12.imprint","INTERSECT",VERTEX,{"derivedFrom":[subQ1,subQ0]});Q4=makeQuery(id+"F12.imprint","IMPRINT",FACE,{"disambiguationData":[TD([[makeQuery(id+"F12.imprint","IMPRINT",EDGE,{"disambiguationData":[TD([[subQ2,-1.0]])],"derivedFrom":subQ1}),-1.0]])]});}
            var Q5;
            {var subQ0=sQuery(id+"F12.wireOp",EDGE,"E98");var subQ1=sQuery(id+"F12.wireOp",EDGE,"E90");var subQ2=makeQuery(id+"F12.imprint","INTERSECT",VERTEX,{"disambiguationData":[OD(0.0)],"derivedFrom":[subQ1,subQ0]});Q5=makeQuery(id+"F12.imprint","IMPRINT",FACE,{"disambiguationData":[TD([[makeQuery(id+"F12.imprint","IMPRINT",EDGE,{"disambiguationData":[TD([[subQ2,-1.0]])],"derivedFrom":subQ1}),-1.0]])]});}
            var Q6;
            {var subQ0=sQuery(id+"F12.wireOp",EDGE,"E98");var subQ1=sQuery(id+"F12.wireOp",EDGE,"E90");var subQ2=makeQuery(id+"F12.imprint","INTERSECT",VERTEX,{"disambiguationData":[OD(0.0)],"derivedFrom":[subQ1,subQ0]});Q6=makeQuery(id+"F12.imprint","IMPRINT",FACE,{"disambiguationData":[TD([[makeQuery(id+"F12.imprint","IMPRINT",EDGE,{"disambiguationData":[TD([[subQ2,-1.0]])],"derivedFrom":subQ1}),1.0]])]});}
            var Q7;
            {var subQ0=sQuery(id+"F12.wireOp",EDGE,"E92");var subQ1=sQuery(id+"F12.wireOp",EDGE,"E90");var subQ2=makeQuery(id+"F12.imprint","INTERSECT",VERTEX,{"derivedFrom":[subQ1,subQ0]});Q7=makeQuery(id+"F12.imprint","IMPRINT",FACE,{"disambiguationData":[TD([[makeQuery(id+"F12.imprint","IMPRINT",EDGE,{"disambiguationData":[TD([[subQ2,-1.0]])],"derivedFrom":subQ1}),1.0]])]});}
            var Q8;
            {var subQ0=sQuery(id+"F12.wireOp",EDGE,"E91");var subQ1=sQuery(id+"F12.wireOp",EDGE,"E90");var subQ2=makeQuery(id+"F12.imprint","INTERSECT",VERTEX,{"derivedFrom":[subQ1,subQ0]});Q8=makeQuery(id+"F12.imprint","IMPRINT",FACE,{"disambiguationData":[TD([[makeQuery(id+"F12.imprint","IMPRINT",EDGE,{"disambiguationData":[TD([[subQ2,-1.0]])],"derivedFrom":subQ1}),-1.0]])]});}
            var Q9;
            {var subQ0=sQuery(id+"F12.wireOp",EDGE,"E99");var subQ1=sQuery(id+"F12.wireOp",EDGE,"E90");var subQ2=makeQuery(id+"F12.imprint","INTERSECT",VERTEX,{"disambiguationData":[OD(0.0)],"derivedFrom":[subQ1,subQ0]});Q9=makeQuery(id+"F12.imprint","IMPRINT",FACE,{"disambiguationData":[TD([[makeQuery(id+"F12.imprint","IMPRINT",EDGE,{"disambiguationData":[TD([[subQ2,-1.0]])],"derivedFrom":subQ1}),-1.0]])]});}
            var Q10;
            {var subQ0=sQuery(id+"F12.wireOp",EDGE,"E99");var subQ1=sQuery(id+"F12.wireOp",EDGE,"E90");var subQ2=makeQuery(id+"F12.imprint","INTERSECT",VERTEX,{"disambiguationData":[OD(0.0)],"derivedFrom":[subQ1,subQ0]});Q10=makeQuery(id+"F12.imprint","IMPRINT",FACE,{"disambiguationData":[TD([[makeQuery(id+"F12.imprint","IMPRINT",EDGE,{"disambiguationData":[TD([[subQ2,-1.0]])],"derivedFrom":subQ1}),1.0]])]});}
            var Q11;
            {var subQ0=sQuery(id+"F12.wireOp",EDGE,"E91");var subQ1=sQuery(id+"F12.wireOp",EDGE,"E90");var subQ2=makeQuery(id+"F12.imprint","INTERSECT",VERTEX,{"derivedFrom":[subQ1,subQ0]});Q11=makeQuery(id+"F12.imprint","IMPRINT",FACE,{"disambiguationData":[TD([[makeQuery(id+"F12.imprint","IMPRINT",EDGE,{"disambiguationData":[TD([[subQ2,-1.0]])],"derivedFrom":subQ1}),1.0]])]});}
            var Q12;
            {var subQ0=sQuery(id+"F12.wireOp",EDGE,"E104");var subQ1=sQuery(id+"F12.wireOp",EDGE,"E90");var subQ2=makeQuery(id+"F12.imprint","INTERSECT",VERTEX,{"disambiguationData":[OD(0.0)],"derivedFrom":[subQ1,subQ0]});Q12=makeQuery(id+"F12.imprint","IMPRINT",FACE,{"disambiguationData":[TD([[makeQuery(id+"F12.imprint","IMPRINT",EDGE,{"disambiguationData":[TD([[subQ2,-1.0]])],"derivedFrom":subQ1}),-1.0]])]});}
            var Q13;
            {var subQ0=sQuery(id+"F12.wireOp",EDGE,"E100");var subQ1=sQuery(id+"F12.wireOp",EDGE,"E90");var subQ2=makeQuery(id+"F12.imprint","INTERSECT",VERTEX,{"derivedFrom":[subQ1,subQ0]});Q13=makeQuery(id+"F12.imprint","IMPRINT",FACE,{"disambiguationData":[TD([[makeQuery(id+"F12.imprint","IMPRINT",EDGE,{"disambiguationData":[TD([[subQ2,-1.0]])],"derivedFrom":subQ1}),-1.0]])]});}
            var Q14;
            {var subQ0=sQuery(id+"F12.wireOp",EDGE,"E100");var subQ1=sQuery(id+"F12.wireOp",EDGE,"E90");var subQ2=makeQuery(id+"F12.imprint","INTERSECT",VERTEX,{"derivedFrom":[subQ1,subQ0]});Q14=makeQuery(id+"F12.imprint","IMPRINT",FACE,{"disambiguationData":[TD([[makeQuery(id+"F12.imprint","IMPRINT",EDGE,{"disambiguationData":[TD([[subQ2,-1.0]])],"derivedFrom":subQ1}),1.0]])]});}
            var Q15;
            {var subQ0=sQuery(id+"F12.wireOp",EDGE,"E104");var subQ1=sQuery(id+"F12.wireOp",EDGE,"E90");var subQ2=makeQuery(id+"F12.imprint","INTERSECT",VERTEX,{"disambiguationData":[OD(0.0)],"derivedFrom":[subQ1,subQ0]});Q15=makeQuery(id+"F12.imprint","IMPRINT",FACE,{"disambiguationData":[TD([[makeQuery(id+"F12.imprint","IMPRINT",EDGE,{"disambiguationData":[TD([[subQ2,-1.0]])],"derivedFrom":subQ1}),1.0]])]});}
            var Q16;
            {var subQ0=sQuery(id+"F12.wireOp",EDGE,"E101");var subQ1=sQuery(id+"F12.wireOp",EDGE,"E90");var subQ2=makeQuery(id+"F12.imprint","INTERSECT",VERTEX,{"derivedFrom":[subQ1,subQ0]});Q16=makeQuery(id+"F12.imprint","IMPRINT",FACE,{"disambiguationData":[TD([[makeQuery(id+"F12.imprint","IMPRINT",EDGE,{"disambiguationData":[TD([[subQ2,-1.0]])],"derivedFrom":subQ1}),1.0]])]});}
            var Q17;
            {var subQ0=sQuery(id+"F12.wireOp",EDGE,"E105");var subQ1=sQuery(id+"F12.wireOp",EDGE,"E90");var subQ2=makeQuery(id+"F12.imprint","INTERSECT",VERTEX,{"disambiguationData":[OD(0.0)],"derivedFrom":[subQ1,subQ0]});Q17=makeQuery(id+"F12.imprint","IMPRINT",FACE,{"disambiguationData":[TD([[makeQuery(id+"F12.imprint","IMPRINT",EDGE,{"disambiguationData":[TD([[subQ2,-1.0]])],"derivedFrom":subQ1}),1.0]])]});}
            var Q18;
            {var subQ0=sQuery(id+"F12.wireOp",EDGE,"E105");var subQ1=sQuery(id+"F12.wireOp",EDGE,"E90");var subQ2=makeQuery(id+"F12.imprint","INTERSECT",VERTEX,{"disambiguationData":[OD(0.0)],"derivedFrom":[subQ1,subQ0]});Q18=makeQuery(id+"F12.imprint","IMPRINT",FACE,{"disambiguationData":[TD([[makeQuery(id+"F12.imprint","IMPRINT",EDGE,{"disambiguationData":[TD([[subQ2,-1.0]])],"derivedFrom":subQ1}),-1.0]])]});}
            var Q19;
            {var subQ0=sQuery(id+"F12.wireOp",EDGE,"E101");var subQ1=sQuery(id+"F12.wireOp",EDGE,"E90");var subQ2=makeQuery(id+"F12.imprint","INTERSECT",VERTEX,{"derivedFrom":[subQ1,subQ0]});Q19=makeQuery(id+"F12.imprint","IMPRINT",FACE,{"disambiguationData":[TD([[makeQuery(id+"F12.imprint","IMPRINT",EDGE,{"disambiguationData":[TD([[subQ2,-1.0]])],"derivedFrom":subQ1}),-1.0]])]});}
            extrude(context, id + "F13", {"entities" : qUnion([Q0, Q1, Q2, Q3, Q4, Q5, Q6, Q7, Q8, Q9, Q10, Q11, Q12, Q13, Q14, Q15, Q16, Q17, Q18, Q19]), "operationType" : NewBodyOperationType.REMOVE, "oppositeDirection" : true, "depth" : 2.4 * mm, "offsetDistance" : 25 * mm});
        }
        {
            var Q0;
            {var subQ0=sQuery(id+"F11.wireOp",EDGE,"E82");var subQ1=sQuery(id+"F11.wireOp",EDGE,"E74");var subQ2=makeQuery(id+"F11.imprint","INTERSECT",VERTEX,{"disambiguationData":[OD(0.0)],"derivedFrom":[subQ1,subQ0]});Q0=makeQuery(id+"F11.imprint","IMPRINT",FACE,{"disambiguationData":[TD([[makeQuery(id+"F11.imprint","IMPRINT",EDGE,{"disambiguationData":[TD([[subQ2,-1.0]])],"derivedFrom":subQ1}),1.0]])]});}
            var Q1;
            {var subQ0=sQuery(id+"F11.wireOp",EDGE,"E76");var subQ1=sQuery(id+"F11.wireOp",EDGE,"E74");var subQ2=makeQuery(id+"F11.imprint","INTERSECT",VERTEX,{"derivedFrom":[subQ1,subQ0]});Q1=makeQuery(id+"F11.imprint","IMPRINT",FACE,{"disambiguationData":[TD([[makeQuery(id+"F11.imprint","IMPRINT",EDGE,{"disambiguationData":[TD([[subQ2,-1.0]])],"derivedFrom":subQ1}),1.0]])]});}
            var Q2;
            {var subQ0=sQuery(id+"F11.wireOp",EDGE,"E76");var subQ1=sQuery(id+"F11.wireOp",EDGE,"E74");var subQ2=makeQuery(id+"F11.imprint","INTERSECT",VERTEX,{"derivedFrom":[subQ1,subQ0]});Q2=makeQuery(id+"F11.imprint","IMPRINT",FACE,{"disambiguationData":[TD([[makeQuery(id+"F11.imprint","IMPRINT",EDGE,{"disambiguationData":[TD([[subQ2,-1.0]])],"derivedFrom":subQ1}),-1.0]])]});}
            var Q3;
            {var subQ0=sQuery(id+"F11.wireOp",EDGE,"E82");var subQ1=sQuery(id+"F11.wireOp",EDGE,"E74");var subQ2=makeQuery(id+"F11.imprint","INTERSECT",VERTEX,{"disambiguationData":[OD(0.0)],"derivedFrom":[subQ1,subQ0]});Q3=makeQuery(id+"F11.imprint","IMPRINT",FACE,{"disambiguationData":[TD([[makeQuery(id+"F11.imprint","IMPRINT",EDGE,{"disambiguationData":[TD([[subQ2,-1.0]])],"derivedFrom":subQ1}),-1.0]])]});}
            var Q4;
            {var subQ0=sQuery(id+"F11.wireOp",EDGE,"E77");var subQ1=sQuery(id+"F11.wireOp",EDGE,"E74");var subQ2=makeQuery(id+"F11.imprint","INTERSECT",VERTEX,{"derivedFrom":[subQ1,subQ0]});Q4=makeQuery(id+"F11.imprint","IMPRINT",FACE,{"disambiguationData":[TD([[makeQuery(id+"F11.imprint","IMPRINT",EDGE,{"disambiguationData":[TD([[subQ2,-1.0]])],"derivedFrom":subQ1}),1.0]])]});}
            var Q5;
            {var subQ0=sQuery(id+"F11.wireOp",EDGE,"E81");var subQ1=sQuery(id+"F11.wireOp",EDGE,"E74");var subQ2=makeQuery(id+"F11.imprint","INTERSECT",VERTEX,{"disambiguationData":[OD(0.0)],"derivedFrom":[subQ1,subQ0]});Q5=makeQuery(id+"F11.imprint","IMPRINT",FACE,{"disambiguationData":[TD([[makeQuery(id+"F11.imprint","IMPRINT",EDGE,{"disambiguationData":[TD([[subQ2,-1.0]])],"derivedFrom":subQ1}),1.0]])]});}
            var Q6;
            {var subQ0=sQuery(id+"F11.wireOp",EDGE,"E81");var subQ1=sQuery(id+"F11.wireOp",EDGE,"E74");var subQ2=makeQuery(id+"F11.imprint","INTERSECT",VERTEX,{"disambiguationData":[OD(0.0)],"derivedFrom":[subQ1,subQ0]});Q6=makeQuery(id+"F11.imprint","IMPRINT",FACE,{"disambiguationData":[TD([[makeQuery(id+"F11.imprint","IMPRINT",EDGE,{"disambiguationData":[TD([[subQ2,-1.0]])],"derivedFrom":subQ1}),-1.0]])]});}
            var Q7;
            {var subQ0=sQuery(id+"F11.wireOp",EDGE,"E77");var subQ1=sQuery(id+"F11.wireOp",EDGE,"E74");var subQ2=makeQuery(id+"F11.imprint","INTERSECT",VERTEX,{"derivedFrom":[subQ1,subQ0]});Q7=makeQuery(id+"F11.imprint","IMPRINT",FACE,{"disambiguationData":[TD([[makeQuery(id+"F11.imprint","IMPRINT",EDGE,{"disambiguationData":[TD([[subQ2,-1.0]])],"derivedFrom":subQ1}),-1.0]])]});}
            var Q8;
            {var subQ0=sQuery(id+"F11.wireOp",EDGE,"E75");var subQ1=sQuery(id+"F11.wireOp",EDGE,"E74");var subQ2=makeQuery(id+"F11.imprint","INTERSECT",VERTEX,{"derivedFrom":[subQ1,subQ0]});Q8=makeQuery(id+"F11.imprint","IMPRINT",FACE,{"disambiguationData":[TD([[makeQuery(id+"F11.imprint","IMPRINT",EDGE,{"disambiguationData":[TD([[subQ2,-1.0]])],"derivedFrom":subQ1}),1.0]])]});}
            var Q9;
            {var subQ0=sQuery(id+"F11.wireOp",EDGE,"E83");var subQ1=sQuery(id+"F11.wireOp",EDGE,"E74");var subQ2=makeQuery(id+"F11.imprint","INTERSECT",VERTEX,{"disambiguationData":[OD(0.0)],"derivedFrom":[subQ1,subQ0]});Q9=makeQuery(id+"F11.imprint","IMPRINT",FACE,{"disambiguationData":[TD([[makeQuery(id+"F11.imprint","IMPRINT",EDGE,{"disambiguationData":[TD([[subQ2,-1.0]])],"derivedFrom":subQ1}),1.0]])]});}
            var Q10;
            {var subQ0=sQuery(id+"F11.wireOp",EDGE,"E83");var subQ1=sQuery(id+"F11.wireOp",EDGE,"E74");var subQ2=makeQuery(id+"F11.imprint","INTERSECT",VERTEX,{"disambiguationData":[OD(0.0)],"derivedFrom":[subQ1,subQ0]});Q10=makeQuery(id+"F11.imprint","IMPRINT",FACE,{"disambiguationData":[TD([[makeQuery(id+"F11.imprint","IMPRINT",EDGE,{"disambiguationData":[TD([[subQ2,-1.0]])],"derivedFrom":subQ1}),-1.0]])]});}
            var Q11;
            {var subQ0=sQuery(id+"F11.wireOp",EDGE,"E75");var subQ1=sQuery(id+"F11.wireOp",EDGE,"E74");var subQ2=makeQuery(id+"F11.imprint","INTERSECT",VERTEX,{"derivedFrom":[subQ1,subQ0]});Q11=makeQuery(id+"F11.imprint","IMPRINT",FACE,{"disambiguationData":[TD([[makeQuery(id+"F11.imprint","IMPRINT",EDGE,{"disambiguationData":[TD([[subQ2,-1.0]])],"derivedFrom":subQ1}),-1.0]])]});}
            var Q12;
            {var subQ0=sQuery(id+"F11.wireOp",EDGE,"E85");var subQ1=sQuery(id+"F11.wireOp",EDGE,"E74");var subQ2=makeQuery(id+"F11.imprint","INTERSECT",VERTEX,{"derivedFrom":[subQ1,subQ0]});Q12=makeQuery(id+"F11.imprint","IMPRINT",FACE,{"disambiguationData":[TD([[makeQuery(id+"F11.imprint","IMPRINT",EDGE,{"disambiguationData":[TD([[subQ2,-1.0]])],"derivedFrom":subQ1}),1.0]])]});}
            var Q13;
            {var subQ0=sQuery(id+"F11.wireOp",EDGE,"E88");var subQ1=sQuery(id+"F11.wireOp",EDGE,"E74");var subQ2=makeQuery(id+"F11.imprint","INTERSECT",VERTEX,{"disambiguationData":[OD(0.0)],"derivedFrom":[subQ1,subQ0]});Q13=makeQuery(id+"F11.imprint","IMPRINT",FACE,{"disambiguationData":[TD([[makeQuery(id+"F11.imprint","IMPRINT",EDGE,{"disambiguationData":[TD([[subQ2,-1.0]])],"derivedFrom":subQ1}),1.0]])]});}
            var Q14;
            {var subQ0=sQuery(id+"F11.wireOp",EDGE,"E88");var subQ1=sQuery(id+"F11.wireOp",EDGE,"E74");var subQ2=makeQuery(id+"F11.imprint","INTERSECT",VERTEX,{"disambiguationData":[OD(0.0)],"derivedFrom":[subQ1,subQ0]});Q14=makeQuery(id+"F11.imprint","IMPRINT",FACE,{"disambiguationData":[TD([[makeQuery(id+"F11.imprint","IMPRINT",EDGE,{"disambiguationData":[TD([[subQ2,-1.0]])],"derivedFrom":subQ1}),-1.0]])]});}
            var Q15;
            {var subQ0=sQuery(id+"F11.wireOp",EDGE,"E85");var subQ1=sQuery(id+"F11.wireOp",EDGE,"E74");var subQ2=makeQuery(id+"F11.imprint","INTERSECT",VERTEX,{"derivedFrom":[subQ1,subQ0]});Q15=makeQuery(id+"F11.imprint","IMPRINT",FACE,{"disambiguationData":[TD([[makeQuery(id+"F11.imprint","IMPRINT",EDGE,{"disambiguationData":[TD([[subQ2,-1.0]])],"derivedFrom":subQ1}),-1.0]])]});}
            var Q16;
            {var subQ0=sQuery(id+"F11.wireOp",EDGE,"E84");var subQ1=sQuery(id+"F11.wireOp",EDGE,"E74");var subQ2=makeQuery(id+"F11.imprint","INTERSECT",VERTEX,{"derivedFrom":[subQ1,subQ0]});Q16=makeQuery(id+"F11.imprint","IMPRINT",FACE,{"disambiguationData":[TD([[makeQuery(id+"F11.imprint","IMPRINT",EDGE,{"disambiguationData":[TD([[subQ2,-1.0]])],"derivedFrom":subQ1}),1.0]])]});}
            var Q17;
            {var subQ0=sQuery(id+"F11.wireOp",EDGE,"E84");var subQ1=sQuery(id+"F11.wireOp",EDGE,"E74");var subQ2=makeQuery(id+"F11.imprint","INTERSECT",VERTEX,{"derivedFrom":[subQ1,subQ0]});Q17=makeQuery(id+"F11.imprint","IMPRINT",FACE,{"disambiguationData":[TD([[makeQuery(id+"F11.imprint","IMPRINT",EDGE,{"disambiguationData":[TD([[subQ2,-1.0]])],"derivedFrom":subQ1}),-1.0]])]});}
            var Q18;
            {var subQ0=sQuery(id+"F11.wireOp",EDGE,"E89");var subQ1=sQuery(id+"F11.wireOp",EDGE,"E74");var subQ2=makeQuery(id+"F11.imprint","INTERSECT",VERTEX,{"disambiguationData":[OD(0.0)],"derivedFrom":[subQ1,subQ0]});Q18=makeQuery(id+"F11.imprint","IMPRINT",FACE,{"disambiguationData":[TD([[makeQuery(id+"F11.imprint","IMPRINT",EDGE,{"disambiguationData":[TD([[subQ2,-1.0]])],"derivedFrom":subQ1}),-1.0]])]});}
            var Q19;
            {var subQ0=sQuery(id+"F11.wireOp",EDGE,"E89");var subQ1=sQuery(id+"F11.wireOp",EDGE,"E74");var subQ2=makeQuery(id+"F11.imprint","INTERSECT",VERTEX,{"disambiguationData":[OD(0.0)],"derivedFrom":[subQ1,subQ0]});Q19=makeQuery(id+"F11.imprint","IMPRINT",FACE,{"disambiguationData":[TD([[makeQuery(id+"F11.imprint","IMPRINT",EDGE,{"disambiguationData":[TD([[subQ2,-1.0]])],"derivedFrom":subQ1}),1.0]])]});}
            extrude(context, id + "F14", {"entities" : qUnion([Q0, Q1, Q2, Q3, Q4, Q5, Q6, Q7, Q8, Q9, Q10, Q11, Q12, Q13, Q14, Q15, Q16, Q17, Q18, Q19]), "operationType" : NewBodyOperationType.ADD, "depth" : 2.2 * mm, "offsetDistance" : 25 * mm});
        }
    });
